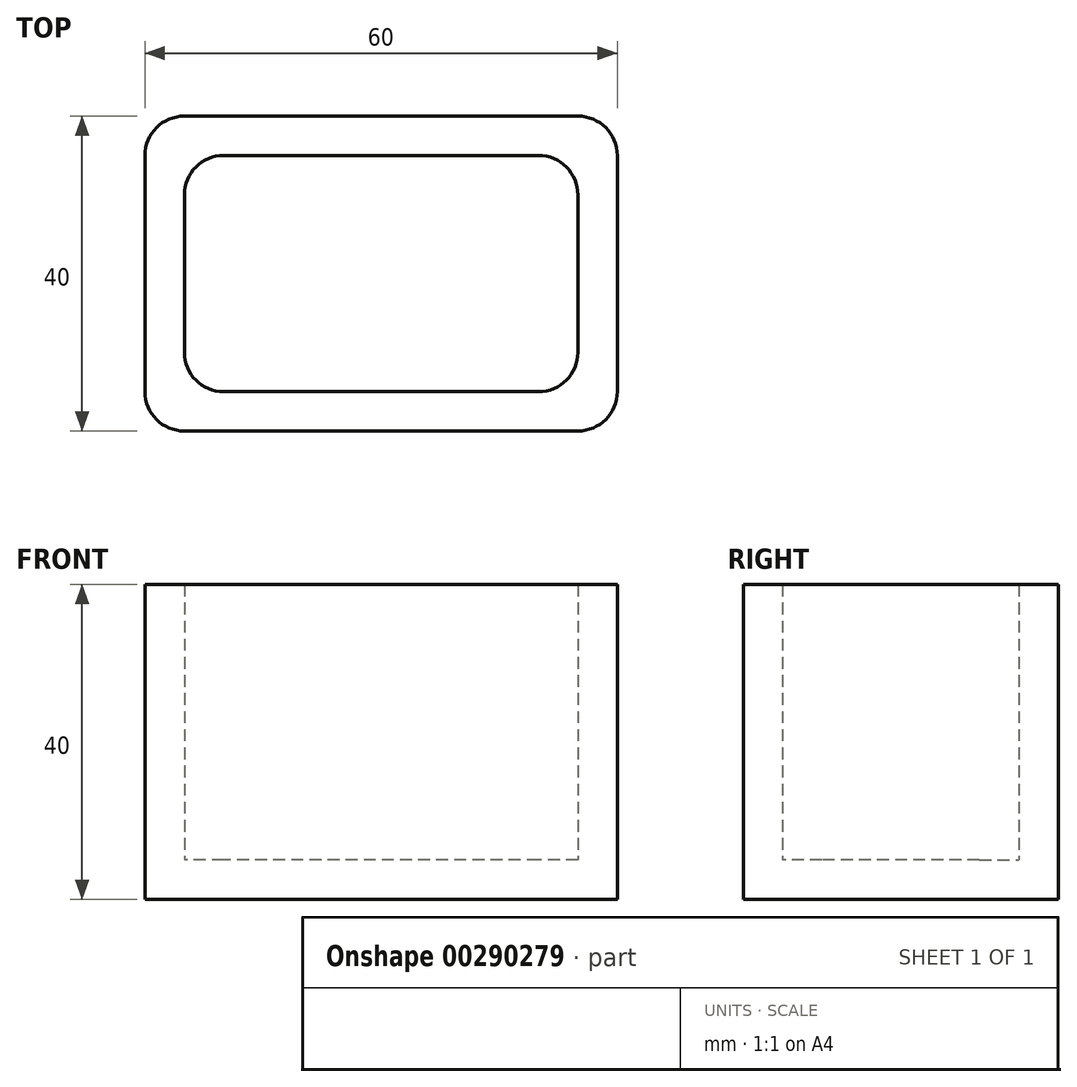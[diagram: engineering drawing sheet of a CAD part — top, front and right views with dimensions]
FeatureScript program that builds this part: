
annotation { "Feature Type Name" : "Feature", "Feature Type Description" : "" }
export const myFeature = defineFeature(function(context is Context, id is Id, definition is map)
    precondition{}
    {
        {
            var Q0;
            Q0=qCreatedBy(makeId("Top.planeOp"),FACE);
            var sketch = newSketch(context, id + "F0", { "sketchPlane" : qUnion([Q0])});
            skLineSegment(sketch, "E0.bottom", {"start": v(30, 20) * mm, "end": v(-30, 20) * mm});
            skLineSegment(sketch, "E0.top", {"start": v(30, -20) * mm, "end": v(-30, -20) * mm});
            skLineSegment(sketch, "E0.left", {"start": v(30, 20) * mm, "end": v(30, -20) * mm});
            skLineSegment(sketch, "E0.right", {"start": v(-30, 20) * mm, "end": v(-30, -20) * mm});
            skPoint(sketch, "E0.middle", {"position": v(0, 0) * mm});
            skSolve(sketch);
        }
        {
            var Q0;
            Q0 = qSketchRegion(id + "F0", true);
            extrude(context, id + "F1", {"entities" : qUnion([Q0]), "depth" : 40 * mm});
        }
        {
            var Q0;
            Q0=makeQuery(id+"F1.opExtrude","CAP_FACE",FACE,{"disambiguationData":[OSD([sQuery(id+"F0.wireOp",EDGE,"E0.bottom"),sQuery(id+"F0.wireOp",EDGE,"E0.top"),sQuery(id+"F0.wireOp",EDGE,"E0.left"),sQuery(id+"F0.wireOp",EDGE,"E0.right")])],"isStart":false});
            shell(context, id + "F2", {"entities" : qUnion([Q0]), "thickness" : 5 * mm});
        }
        {
            var Q0;
            Q0=makeQuery(id+"F2.opShell","OFFSET_EDGE",EDGE,{"disambiguationData":[OSD([sQuery(id+"F0.wireOp",EDGE,"E0.bottom"),sQuery(id+"F0.wireOp",EDGE,"E0.right")])]});
            var Q1;
            Q1=makeQuery(id+"F1.opExtrude","SWEPT_EDGE",EDGE,{"disambiguationData":[OSD([sQuery(id+"F0.wireOp",EDGE,"E0.top"),sQuery(id+"F0.wireOp",EDGE,"E0.right")])]});
            var Q2;
            Q2=makeQuery(id+"F1.opExtrude","SWEPT_EDGE",EDGE,{"disambiguationData":[OSD([sQuery(id+"F0.wireOp",EDGE,"E0.top"),sQuery(id+"F0.wireOp",EDGE,"E0.left")])]});
            var Q3;
            Q3=makeQuery(id+"F1.opExtrude","SWEPT_EDGE",EDGE,{"disambiguationData":[OSD([sQuery(id+"F0.wireOp",EDGE,"E0.bottom"),sQuery(id+"F0.wireOp",EDGE,"E0.left")])]});
            var Q4;
            Q4=makeQuery(id+"F1.opExtrude","SWEPT_EDGE",EDGE,{"disambiguationData":[OSD([sQuery(id+"F0.wireOp",EDGE,"E0.bottom"),sQuery(id+"F0.wireOp",EDGE,"E0.right")])]});
            var Q5;
            Q5=makeQuery(id+"F2.opShell","OFFSET_EDGE",EDGE,{"disambiguationData":[OSD([sQuery(id+"F0.wireOp",EDGE,"E0.top"),sQuery(id+"F0.wireOp",EDGE,"E0.right")])]});
            var Q6;
            Q6=makeQuery(id+"F2.opShell","OFFSET_EDGE",EDGE,{"disambiguationData":[OSD([sQuery(id+"F0.wireOp",EDGE,"E0.top"),sQuery(id+"F0.wireOp",EDGE,"E0.left")])]});
            var Q7;
            Q7=makeQuery(id+"F2.opShell","OFFSET_EDGE",EDGE,{"disambiguationData":[OSD([sQuery(id+"F0.wireOp",EDGE,"E0.bottom"),sQuery(id+"F0.wireOp",EDGE,"E0.left")])]});
            fillet(context, id + "F3", {"entities" : qUnion([Q0, Q1, Q2, Q3, Q4, Q5, Q6, Q7]), "radius" : 5 * mm, "tangentPropagation" : true, "allowEdgeOverflow" : false});
        }
    });
